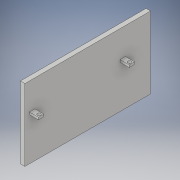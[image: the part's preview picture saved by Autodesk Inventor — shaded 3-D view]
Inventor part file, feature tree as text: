
AUTODESK INVENTOR PART (.ipt)
format: ipt  version: 2019 (Build 230136000, 136)  size: 157,184 bytes
history: native  units: in
note: dims shown in document units (in); Inventor stores cm internally (conversion verified against a paired STEP export)
features: sketch x4, extrude x3, projected_geometry x2, hole x1
ambient origin geometry x8: Origin, YZ Plane, XZ Plane, XY Plane, X Axis, Y Axis, Z Axis, Center Point
bodies: Solid1 (feature_tree)
feature tree (10):
  extrude  "Extrusion1"  Depth=7.0in
  extrude  "Extrusion2"  Depth=1.5in
  hole  "Hole1"  [1 undecoded]
  extrude  "Extrusion4"  Depth=0.125in TaperAngle=0.0deg
  sketch  "Sketch1"  dims[d0=4.0in d1=7.0in]
  sketch  "Sketch2"  dims[d2=0.25in d3=0.0in d4=1.5in]
  sketch  "Sketch3"  dims[d5=1.5in d6=0.125in]
  projected_geometry  "Projected Loop1"
  projected_geometry  "Projected Loop2"
  sketch  "Sketch4"  dims[d7=0.125in d8=0.5in d9=0.0in d10=5.039in d11=5.05in d12=0.3in d13=0.3in d15=0.15in d16=0.5in d17=0.3in d20=0.1875in d21=0.75in d22=0.375in d23=0.25in d24=0.5635in d25=1.0in d26=0.8108in d28=0.125in d29=0.125in d30=0.25in d33=0.125in d34=0.0in]
note: 1 required parameter value undecoded (feature->parameter linkage not recoverable at this tier; creation-order binding heuristic only, values carry confidence <= 0.55)
